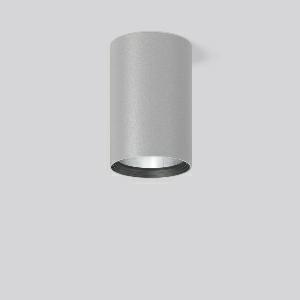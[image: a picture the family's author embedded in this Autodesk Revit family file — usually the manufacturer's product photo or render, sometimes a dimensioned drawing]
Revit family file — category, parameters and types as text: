
# Revit family: heledon_maxi_a_931226_004_3_76_0bef
name_source: partatom
category: Lighting Fixtures
units: mm (PartAtom-declared; Revit-internal decimal feet)

## family parameters
Cut with Voids When Loaded = No
Host = Face
Light Source = No
Part Type = Normal
Room Calculation Point = No
Round Connector Dimension = Use Diameter
Shared = No

## types (1)
- HELEDON maxi A (1 x LED Modul 935, 4200 lm, 3500)
    Apparent Load = 35 VA
    Approval mark = CE
    CIE Flux Codes = 97 100 100 100 100
    Color Rendering = 92
    Color Temperature = 3500
    Default Elevation = 1800 mm
    Description = Series: HELEDON maxi
Cylindrical surface-mounted downlight. Housing: die-cast aluminium, powder-coated. Internal ceiling frame polycarbonate with bayonet mounting. Black plastic ring and recessed LED to prevent glare from the side. Optical assembly with reflector made of MIRO-Silver with 98% total light reflection for outstanding efficiency - can be changed without tools. Best colour rendering index Ra>90. Suitable for Ceiling mounting. Easy installation with a separate ceiling frame with bayonet mounting and plug connection. Driver integrated. Connected via plug-in connector. High quality converter without flickering and stroboscopic effect. The following accessories can be mounted without use of tools: interchangeable lenses, decorative glasses, honeycomb louvre, clear and frosted diffusers, white interchangeable plastic ring. 
Colour: silver
Diameter: 123 mm
Height: 183 mm
Lamp: LED
Socket: without socket
Colour temperature: 3500K
Colour rendering index (CRI): 92
System power: 35 W
Rated luminous flux: 4200 lm
Luminous efficiency: 120 lm/W
Control gear: Converter, dimmable, DALI
Protection class: I
Type of protection: IP 20
    Height = 183 mm
    Lamp = 1 x LED Modul 935
    Lamp Light Flux = 4200 lm
    Lamp count = 1
    Length = 123 mm
    Lifetime = 50000 h
    Luminous efficacy = 120 lm/W
    Manufacturer = RZB
    ModVariant = No
    Model = 931226.004.3.76
    Mounting Place = Ceiling
    Mounting Type = Surface mounted
    Number of Poles = 1
    OnlyDefault = Yes
    Power Factor = 1
    Product Name = HELEDON maxi A
    Product group = Surface mounted downlights
    ProductGroupID = 302
    Protection Class = Protection class I
    Protection Degree = IP 20
    RLX_Detail_Level = 1
    RLX_Emergency_Light_Flux = 0 lm
    RLX_Emergency_Type = 0
    RLX_Emergency_Type_DB = No
    RlxData = <blob elided: 100093 chars, md5=964d3036>
    Socket = socket
    Standby Power = 0 W
    System Light Flux = 4200 lm
    System Power = 35 W
    Type Comments = Product without accessories
    Type Image = 931192.004.jpg
    URL = http://relux.com
    VarID = ---
    Voltage = 230 V
    Voltage Range = 220-240 V
    Weight = 0.00 kg
    Width = 0 mm  [stored 0 ft]

note: [stored X ft] marks values corroborated as IEEE doubles in the binary element streams (Revit-internal decimal feet)

## geometry (parser evidence)
native form markers: Blend x4, Sweep x11
no freeform markers — native parametric forms only
